# Revit family: RN 90076 Optifitt-Serra-Muffe
name_source: partatom
category: Rohrformteile
units: mm (PartAtom-declared; Revit-internal decimal feet)

## family parameters
Arbeitsebenenbasiert = Nein
Beim Laden mit Abzugskörper schneiden = Nein
Bemaßung runder Anschluss = Durchmesser verwenden
Gemeinsam genutzt = Nein
Immer vertikal = Ja
Teiletyp = Verbindung

## types (8) — shared parameters
1.010.00.2 Blattnummer der Richtlinie = 29
1.010.00.3 Ausgabedatum (Monat) der Richtlinie = 201308
1.010.00.4 Herstellername = R. Nussbaum AG
1.010.00.5 Revisionsdatum der Datei = 20190521
1.010.00.6 Webadresse des Herstellers = http://www.nussbaum.ch
1.100.00.4 Produktbezeichnung = Versorgung
1.110.00.2 Index = 3
1.110.00.4 Produktbezeichnung = Optifitt-Serra
1.960/3L.00.8 Link (URL) = https://www.nussbaum.ch
29.700.00.4 Produktname = Optifitt-Serra-Muffe
29.700.00.5 Produktkennung = 2
29.700.00.6 Querschnittsform = 1
29.700.00.7 Nennweitensystem = DN
29.700.00.8 Nenndrucksystem = PN
29.710.02.4 Nenndruck = 16
29.710.02.5 max. zul. Überdruck [hPa] = 1600
29.710.02.7 max. zul. Dauer-Betriebsdruck [hPa] = 1600
29.710.02.9 max. zul. Dauer-Betriebstemperatur [°C] = 90
Connector Visibility = Nein
EnclosingSpace Visibility = Nein
Hersteller = R. Nussbaum AG
URL = https://www.nussbaum.ch

## per-type parameters (varying)
- DN=65: 1.800.00.3 TGA-Nummer=01900300000000000000000000000000000000000000000011000000000000000020; 1.800.00.4 Kommentarfeld=90076.10, Optifitt-Serra-Muffe, DN=65, L=64, Rp=2½; 1.810.00.3 Hersteller-Bestellnummer=90076.1; 1.810.00.4 DATANORM-Nummer=90076.1; 1.810.00.5 StLB-Nummer=214.118; 1.810.00.6 GTIN-Nummer=7612945680921; 29.710.02.10 Formstück-Gewicht [kg]=0.549; 29.710.02.3 Benennung=Optifitt-Serra-Muffe, DN=65, L=64, Rp=2½; CONNECTOR0_DIAMETER_dX_0r=65 mm; CONNECTOR0_dX_01=27 mm; CONNECTOR0_ref_dX=27 mm; CONNECTOR1_DIAMETER_dX_0r=65 mm; CONNECTOR1_dX_00=37 mm  [stored 0.121391 ft]; CONNECTOR1_dX_01=64 mm; CONNECTOR1_ref_dX=37 mm  [stored 0.121391 ft]; Modell=90076.1; R. Nussbaum AG 90076.04 de Visibility=Nein; R. Nussbaum AG 90076.05 de Visibility=Nein; R. Nussbaum AG 90076.06 de Visibility=Nein; R. Nussbaum AG 90076.07 de Visibility=Nein; R. Nussbaum AG 90076.08 de Visibility=Nein; R. Nussbaum AG 90076.09 de Visibility=Nein; R. Nussbaum AG 90076.10 de Visibility=Ja; R. Nussbaum AG 90076.11 de Visibility=Nein; Typenkommentare=Optifitt-Serra-Muffe  DN=65
- DN=80: 1.800.00.3 TGA-Nummer=01900300000000000000000000000000000000000000000011000000000000000015; 1.800.00.4 Kommentarfeld=90076.11, Optifitt-Serra-Muffe, DN=80, L=70, Rp=3; 1.810.00.3 Hersteller-Bestellnummer=90076.11; 1.810.00.4 DATANORM-Nummer=90076.11; 1.810.00.6 GTIN-Nummer=7612945680938; 29.710.02.10 Formstück-Gewicht [kg]=0.704; 29.710.02.3 Benennung=Optifitt-Serra-Muffe, DN=80, L=70, Rp=3; CONNECTOR0_DIAMETER_dX_0r=80 mm; CONNECTOR0_dX_01=30 mm; CONNECTOR0_ref_dX=30 mm; CONNECTOR1_DIAMETER_dX_0r=80 mm; CONNECTOR1_dX_00=40 mm; CONNECTOR1_dX_01=70 mm; CONNECTOR1_ref_dX=40 mm; Modell=90076.11; R. Nussbaum AG 90076.04 de Visibility=Nein; R. Nussbaum AG 90076.05 de Visibility=Nein; R. Nussbaum AG 90076.06 de Visibility=Nein; R. Nussbaum AG 90076.07 de Visibility=Nein; R. Nussbaum AG 90076.08 de Visibility=Nein; R. Nussbaum AG 90076.09 de Visibility=Nein; R. Nussbaum AG 90076.10 de Visibility=Nein; R. Nussbaum AG 90076.11 de Visibility=Ja; Typenkommentare=Optifitt-Serra-Muffe  DN=80
- DN=50: 1.800.00.3 TGA-Nummer=01900300000000000000000000000000000000000000000011000000000000000014; 1.800.00.4 Kommentarfeld=90076.09, Optifitt-Serra-Muffe, DN=50, L=55, Rp=2; 1.810.00.3 Hersteller-Bestellnummer=90076.09; 1.810.00.4 DATANORM-Nummer=90076.09; 1.810.00.5 StLB-Nummer=214.117; 1.810.00.6 GTIN-Nummer=7612945680914; 29.710.02.10 Formstück-Gewicht [kg]=0.359; 29.710.02.3 Benennung=Optifitt-Serra-Muffe, DN=50, L=55, Rp=2; CONNECTOR0_DIAMETER_dX_0r=50 mm; CONNECTOR0_dX_01=24 mm; CONNECTOR0_ref_dX=24 mm; CONNECTOR1_DIAMETER_dX_0r=50 mm; CONNECTOR1_dX_00=31 mm; CONNECTOR1_dX_01=55 mm; CONNECTOR1_ref_dX=31 mm; Modell=90076.09; R. Nussbaum AG 90076.04 de Visibility=Nein; R. Nussbaum AG 90076.05 de Visibility=Nein; R. Nussbaum AG 90076.06 de Visibility=Nein; R. Nussbaum AG 90076.07 de Visibility=Nein; R. Nussbaum AG 90076.08 de Visibility=Nein; R. Nussbaum AG 90076.09 de Visibility=Ja; R. Nussbaum AG 90076.10 de Visibility=Nein; R. Nussbaum AG 90076.11 de Visibility=Nein; Typenkommentare=Optifitt-Serra-Muffe  DN=50
- DN=40: 1.800.00.3 TGA-Nummer=01900300000000000000000000000000000000000000000011000000000000000013; 1.800.00.4 Kommentarfeld=90076.08, Optifitt-Serra-Muffe, DN=40, L=47, Rp=1½; 1.810.00.3 Hersteller-Bestellnummer=90076.08; 1.810.00.4 DATANORM-Nummer=90076.08; 1.810.00.5 StLB-Nummer=214.116; 1.810.00.6 GTIN-Nummer=7612945680907; 29.710.02.10 Formstück-Gewicht [kg]=0.259; 29.710.02.3 Benennung=Optifitt-Serra-Muffe, DN=40, L=47, Rp=1½; CONNECTOR0_DIAMETER_dX_0r=40 mm; CONNECTOR0_dX_01=19 mm; CONNECTOR0_ref_dX=19 mm; CONNECTOR1_DIAMETER_dX_0r=40 mm; CONNECTOR1_dX_00=28 mm; CONNECTOR1_dX_01=47 mm; CONNECTOR1_ref_dX=28 mm; Modell=90076.08; R. Nussbaum AG 90076.04 de Visibility=Nein; R. Nussbaum AG 90076.05 de Visibility=Nein; R. Nussbaum AG 90076.06 de Visibility=Nein; R. Nussbaum AG 90076.07 de Visibility=Nein; R. Nussbaum AG 90076.08 de Visibility=Ja; R. Nussbaum AG 90076.09 de Visibility=Nein; R. Nussbaum AG 90076.10 de Visibility=Nein; R. Nussbaum AG 90076.11 de Visibility=Nein; Typenkommentare=Optifitt-Serra-Muffe  DN=40
- DN=32: 1.800.00.3 TGA-Nummer=01900300000000000000000000000000000000000000000011000000000000000012; 1.800.00.4 Kommentarfeld=90076.07, Optifitt-Serra-Muffe, DN=32, L=46, Rp=1¼; 1.810.00.3 Hersteller-Bestellnummer=90076.07; 1.810.00.4 DATANORM-Nummer=90076.07; 1.810.00.5 StLB-Nummer=214.115; 1.810.00.6 GTIN-Nummer=7612945680594; 29.710.02.10 Formstück-Gewicht [kg]=0.157; 29.710.02.3 Benennung=Optifitt-Serra-Muffe, DN=32, L=46, Rp=1¼; CONNECTOR0_DIAMETER_dX_0r=32 mm; CONNECTOR0_dX_01=19 mm; CONNECTOR0_ref_dX=19 mm; CONNECTOR1_DIAMETER_dX_0r=32 mm; CONNECTOR1_dX_00=27 mm; CONNECTOR1_dX_01=46 mm; CONNECTOR1_ref_dX=27 mm; Modell=90076.07; R. Nussbaum AG 90076.04 de Visibility=Nein; R. Nussbaum AG 90076.05 de Visibility=Nein; R. Nussbaum AG 90076.06 de Visibility=Nein; R. Nussbaum AG 90076.07 de Visibility=Ja; R. Nussbaum AG 90076.08 de Visibility=Nein; R. Nussbaum AG 90076.09 de Visibility=Nein; R. Nussbaum AG 90076.10 de Visibility=Nein; R. Nussbaum AG 90076.11 de Visibility=Nein; Typenkommentare=Optifitt-Serra-Muffe  DN=32
- DN=25: 1.800.00.3 TGA-Nummer=01900300000000000000000000000000000000000000000011000000000000000011; 1.800.00.4 Kommentarfeld=90076.06, Optifitt-Serra-Muffe, DN=25, L=43, Rp=1; 1.810.00.3 Hersteller-Bestellnummer=90076.06; 1.810.00.4 DATANORM-Nummer=90076.06; 1.810.00.5 StLB-Nummer=214.114; 1.810.00.6 GTIN-Nummer=7612945680587; 29.710.02.10 Formstück-Gewicht [kg]=0.15; 29.710.02.3 Benennung=Optifitt-Serra-Muffe, DN=25, L=43, Rp=1; CONNECTOR0_DIAMETER_dX_0r=25 mm; CONNECTOR0_dX_01=17 mm; CONNECTOR0_ref_dX=17 mm; CONNECTOR1_DIAMETER_dX_0r=25 mm; CONNECTOR1_dX_00=26 mm; CONNECTOR1_dX_01=43 mm  [stored 0.141076 ft]; CONNECTOR1_ref_dX=26 mm; Modell=90076.06; R. Nussbaum AG 90076.04 de Visibility=Nein; R. Nussbaum AG 90076.05 de Visibility=Nein; R. Nussbaum AG 90076.06 de Visibility=Ja; R. Nussbaum AG 90076.07 de Visibility=Nein; R. Nussbaum AG 90076.08 de Visibility=Nein; R. Nussbaum AG 90076.09 de Visibility=Nein; R. Nussbaum AG 90076.10 de Visibility=Nein; R. Nussbaum AG 90076.11 de Visibility=Nein; Typenkommentare=Optifitt-Serra-Muffe  DN=25
- DN=20: 1.800.00.3 TGA-Nummer=01900300000000000000000000000000000000000000000011000000000000000010; 1.800.00.4 Kommentarfeld=90076.05, Optifitt-Serra-Muffe, DN=20, L=37, Rp=¾; 1.810.00.3 Hersteller-Bestellnummer=90076.05; 1.810.00.4 DATANORM-Nummer=90076.05; 1.810.00.5 StLB-Nummer=214.113; 1.810.00.6 GTIN-Nummer=7612945680570; 29.710.02.10 Formstück-Gewicht [kg]=0.062; 29.710.02.3 Benennung=Optifitt-Serra-Muffe, DN=20, L=37, Rp=¾; CONNECTOR0_DIAMETER_dX_0r=20 mm; CONNECTOR0_dX_01=15 mm; CONNECTOR0_ref_dX=15 mm; CONNECTOR1_DIAMETER_dX_0r=20 mm; CONNECTOR1_dX_00=22 mm; CONNECTOR1_dX_01=37 mm  [stored 0.121391 ft]; CONNECTOR1_ref_dX=22 mm; Modell=90076.05; R. Nussbaum AG 90076.04 de Visibility=Nein; R. Nussbaum AG 90076.05 de Visibility=Ja; R. Nussbaum AG 90076.06 de Visibility=Nein; R. Nussbaum AG 90076.07 de Visibility=Nein; R. Nussbaum AG 90076.08 de Visibility=Nein; R. Nussbaum AG 90076.09 de Visibility=Nein; R. Nussbaum AG 90076.10 de Visibility=Nein; R. Nussbaum AG 90076.11 de Visibility=Nein; Typenkommentare=Optifitt-Serra-Muffe  DN=20
- DN=15: 1.800.00.3 TGA-Nummer=01900300000000000000000000000000000000000000000011000000000000000009; 1.800.00.4 Kommentarfeld=90076.04, Optifitt-Serra-Muffe, DN=15, L=34, Rp=½; 1.810.00.3 Hersteller-Bestellnummer=90076.04; 1.810.00.4 DATANORM-Nummer=90076.04; 1.810.00.5 StLB-Nummer=214.112; 1.810.00.6 GTIN-Nummer=7612945680563; 29.710.02.10 Formstück-Gewicht [kg]=0.05; 29.710.02.3 Benennung=Optifitt-Serra-Muffe, DN=15, L=34, Rp=½; CONNECTOR0_DIAMETER_dX_0r=15 mm; CONNECTOR0_dX_01=13 mm; CONNECTOR0_ref_dX=13 mm; CONNECTOR1_DIAMETER_dX_0r=15 mm; CONNECTOR1_dX_00=21 mm; CONNECTOR1_dX_01=34 mm; CONNECTOR1_ref_dX=21 mm; Modell=90076.04; R. Nussbaum AG 90076.04 de Visibility=Ja; R. Nussbaum AG 90076.05 de Visibility=Nein; R. Nussbaum AG 90076.06 de Visibility=Nein; R. Nussbaum AG 90076.07 de Visibility=Nein; R. Nussbaum AG 90076.08 de Visibility=Nein; R. Nussbaum AG 90076.09 de Visibility=Nein; R. Nussbaum AG 90076.10 de Visibility=Nein; R. Nussbaum AG 90076.11 de Visibility=Nein; Typenkommentare=Optifitt-Serra-Muffe  DN=15

note: [stored X ft] marks values corroborated as IEEE doubles in the binary element streams (Revit-internal decimal feet)

## geometry (parser evidence)
native form markers: Sweep x1
no freeform markers — native parametric forms only
